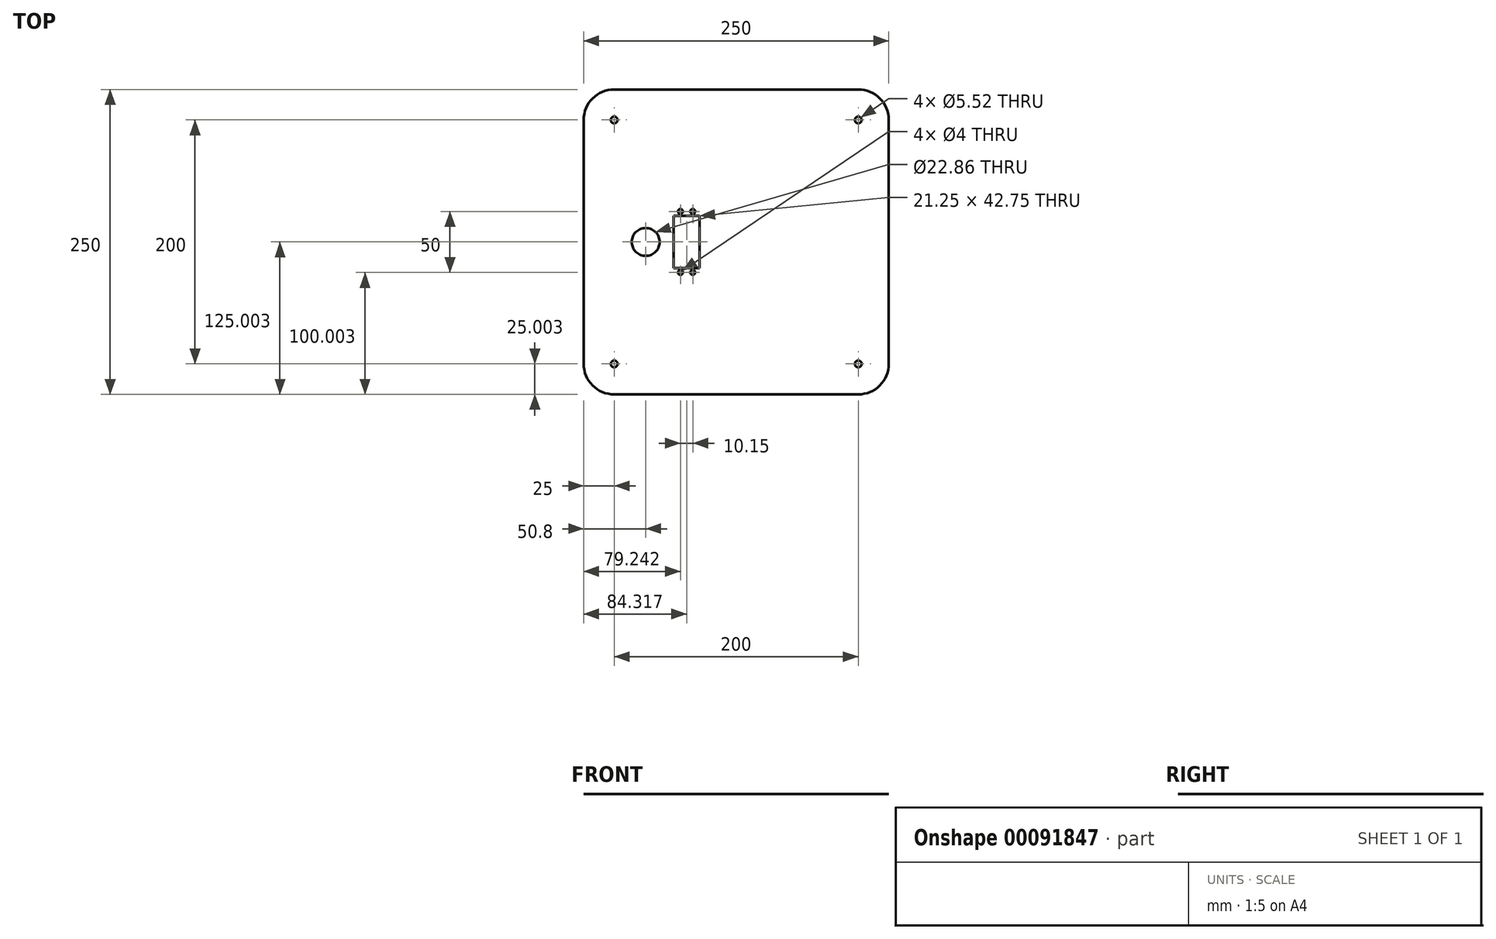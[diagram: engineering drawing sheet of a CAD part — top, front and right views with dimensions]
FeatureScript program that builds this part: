
annotation { "Feature Type Name" : "Feature", "Feature Type Description" : "" }
export const myFeature = defineFeature(function(context is Context, id is Id, definition is map)
    precondition{}
    {
        {
            var Q0;
            Q0=qCreatedBy(makeId("Top.planeOp"),FACE);
            var sketch = newSketch(context, id + "F0", { "sketchPlane" : qUnion([Q0])});
            skLineSegment(sketch, "E0.bottom", {"start": v(-100, 126.2) * mm, "end": v(100, 126.2) * mm});
            skLineSegment(sketch, "E0.top", {"start": v(-100, -123.8) * mm, "end": v(100, -123.8) * mm});
            skLineSegment(sketch, "E0.left", {"start": v(-125, 101.2) * mm, "end": v(-125, -98.8) * mm});
            skLineSegment(sketch, "E0.right", {"start": v(125, 101.2) * mm, "end": v(125, -98.8) * mm});
            skPoint(sketch, "E1.visualSharp", {"position": v(-125, -123.8) * mm});
            skArc(sketch, "E1.filletArc", {"start": v(-125, -98.8) * mm, "mid": v(-117.68, -116.48) * mm, "end": v(-100, -123.8) * mm});
            skPoint(sketch, "E2.visualSharp", {"position": v(-125, 126.2) * mm});
            skArc(sketch, "E2.filletArc", {"start": v(-100, 126.2) * mm, "mid": v(-117.68, 118.87) * mm, "end": v(-125, 101.2) * mm});
            skPoint(sketch, "E3.visualSharp", {"position": v(125, -123.8) * mm});
            skArc(sketch, "E3.filletArc", {"start": v(100, -123.8) * mm, "mid": v(117.68, -116.48) * mm, "end": v(125, -98.8) * mm});
            skPoint(sketch, "E4.visualSharp", {"position": v(125, 126.2) * mm});
            skArc(sketch, "E4.filletArc", {"start": v(125, 101.2) * mm, "mid": v(117.68, 118.87) * mm, "end": v(100, 126.2) * mm});
            skPoint(sketch, "E5", {"position": v(0, -123.8) * mm});
            skLineSegment(sketch, "E6", {"start": v(-125, 1.2) * mm, "end": v(125, 1.2) * mm, "construction": true});
            skLineSegment(sketch, "E7", {"start": v(0, 126.2) * mm, "end": v(0, -123.8) * mm, "construction": true});
            skCircle(sketch, "E8", {"center": v(-100, 101.2) * mm, "radius": 2.76 * mm});
            skCircle(sketch, "E9.MirrorC", {"center": v(100, 101.2) * mm, "radius": 2.76 * mm});
            skCircle(sketch, "E10.MirrorC", {"center": v(100, -98.8) * mm, "radius": 2.76 * mm});
            skCircle(sketch, "E11.MirrorC", {"center": v(-100, -98.8) * mm, "radius": 2.76 * mm});
            skCircle(sketch, "E12", {"center": v(-74.2, 1.2) * mm, "radius": 11.43 * mm});
            skCircle(sketch, "E13", {"center": v(-45.76, 26.2) * mm, "radius": 2 * mm});
            skPoint(sketch, "E14.middle", {"position": v(-20.5, 1.2) * mm});
            skCircle(sketch, "E15", {"center": v(-35.6, 26.2) * mm, "radius": 2 * mm});
            skCircle(sketch, "E16.MirrorC", {"center": v(-45.76, -23.8) * mm, "radius": 2 * mm});
            skCircle(sketch, "E17.MirrorC", {"center": v(-35.6, -23.8) * mm, "radius": 2 * mm});
            skLineSegment(sketch, "E18.bottom", {"start": v(-45.76, 26.2) * mm, "end": v(-35.6, 26.2) * mm, "construction": true});
            skLineSegment(sketch, "E18.top", {"start": v(-45.76, -23.8) * mm, "end": v(-35.6, -23.8) * mm, "construction": true});
            skLineSegment(sketch, "E18.left", {"start": v(-45.76, 26.2) * mm, "end": v(-45.76, -23.8) * mm, "construction": true});
            skLineSegment(sketch, "E18.right", {"start": v(-35.6, 26.2) * mm, "end": v(-35.6, -23.8) * mm, "construction": true});
            skLineSegment(sketch, "E19", {"start": v(-40.68, -23.8) * mm, "end": v(-40.68, 26.2) * mm, "construction": true});
            skLineSegment(sketch, "E20.bottom", {"start": v(-51.3, 22.57) * mm, "end": v(-30.06, 22.57) * mm});
            skLineSegment(sketch, "E20.top", {"start": v(-51.3, -20.18) * mm, "end": v(-30.06, -20.18) * mm});
            skLineSegment(sketch, "E20.left", {"start": v(-51.3, 22.57) * mm, "end": v(-51.3, -20.18) * mm});
            skLineSegment(sketch, "E20.right", {"start": v(-30.06, 22.57) * mm, "end": v(-30.06, -20.18) * mm});
            skPoint(sketch, "E20.middle", {"position": v(-40.68, 1.2) * mm});
            skSolve(sketch);
        }
        {
            var Q0;
            Q0=makeQuery(id+"F0.imprint","IMPRINT",FACE,{"disambiguationData":[TD([[makeQuery(id+"F0.imprint","IMPRINT",EDGE,{"derivedFrom":sQuery(id+"F0.wireOp",EDGE,"E0.bottom")}),-1.0]])]});
            extrude(context, id + "F1", {"entities" : qUnion([Q0]), "depth" : 1 / 203.2 * mm});
        }
    });
